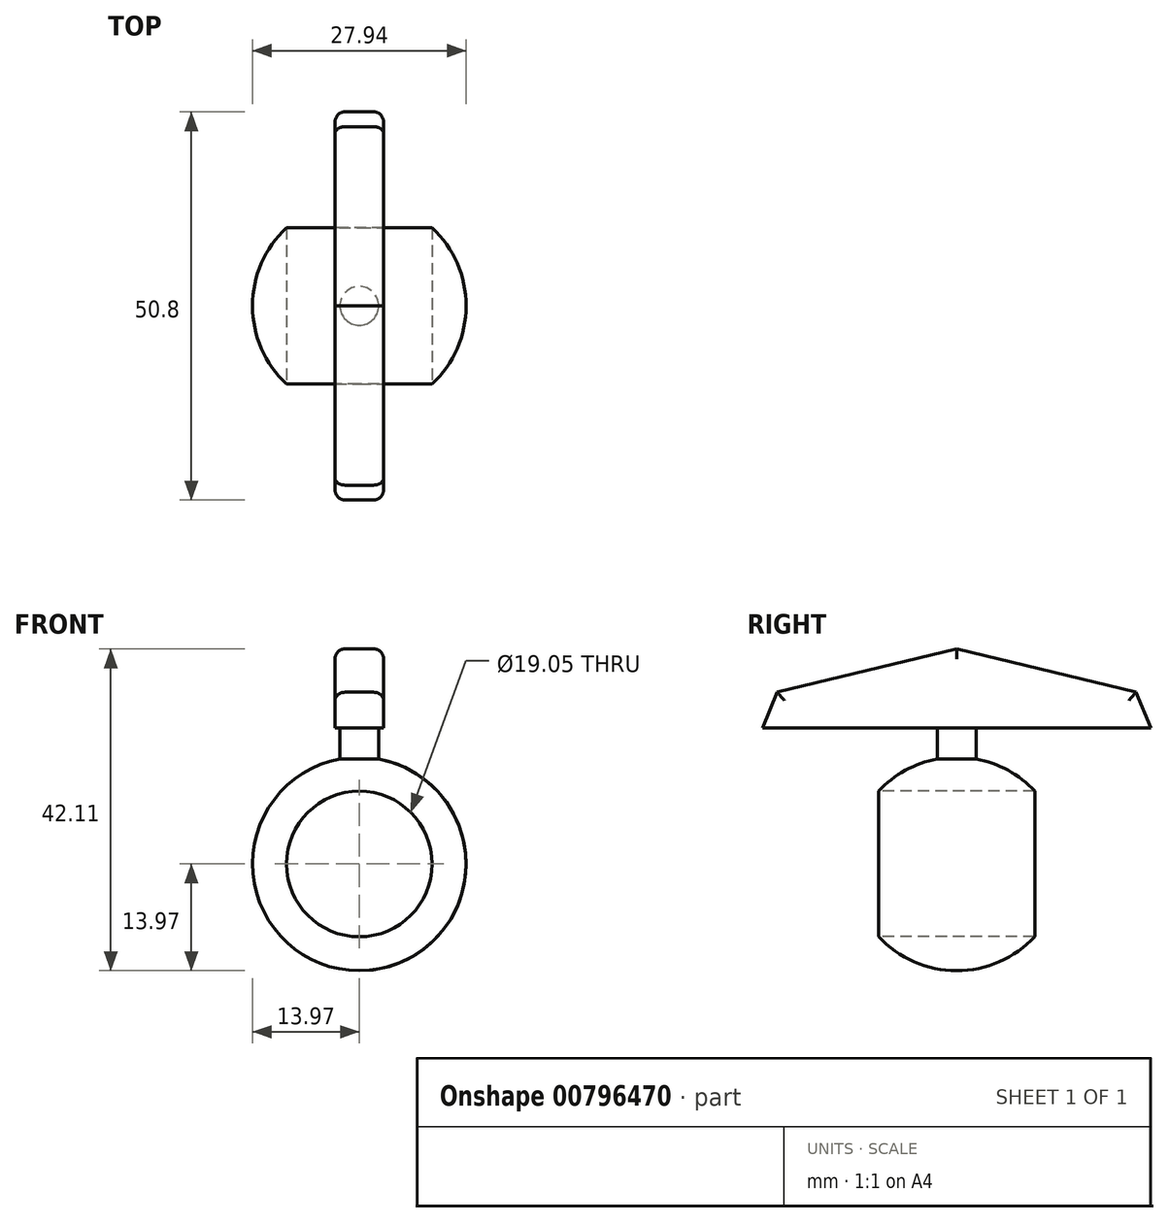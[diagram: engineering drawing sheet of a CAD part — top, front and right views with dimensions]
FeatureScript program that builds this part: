
annotation { "Feature Type Name" : "Feature", "Feature Type Description" : "" }
export const myFeature = defineFeature(function(context is Context, id is Id, definition is map)
    precondition{}
    {
        {
            var Q0;
            Q0=qCreatedBy(makeId("Front.planeOp"),FACE);
            var sketch = newSketch(context, id + "F0", { "sketchPlane" : qUnion([Q0])});
            skLineSegment(sketch, "E0", {"start": v(0, 13.97) * mm, "end": v(0, -13.97) * mm});
            skArc(sketch, "E1", {"start": v(0, -13.97) * mm, "mid": v(13.97, 0) * mm, "end": v(0, 13.97) * mm});
            skLineSegment(sketch, "E2", {"start": v(0, 13.97) * mm, "end": v(0, 17.78) * mm});
            skLineSegment(sketch, "E3", {"start": v(0, 17.78) * mm, "end": v(2.54, 17.78) * mm});
            skLineSegment(sketch, "E4", {"start": v(2.54, 17.78) * mm, "end": v(2.54, 13.74) * mm});
            skSolve(sketch);
        }
        {
            var Q0;
            Q0=qCreatedBy(makeId("Front.planeOp"),FACE);
            var sketch = newSketch(context, id + "F1", { "sketchPlane" : qUnion([Q0])});
            skLineSegment(sketch, "E5", {"start": v(0, 0) * mm, "end": v(0, 12.7) * mm});
            skSolve(sketch);
        }
        {
            var Q0;
            Q0=makeQuery(id+"F0.imprint","IMPRINT",FACE,{"disambiguationData":[TD([[makeQuery(id+"F0.imprint","IMPRINT",EDGE,{"derivedFrom":sQuery(id+"F0.wireOp",EDGE,"E0")}),1.0]])]});
            var Q1;
            {var subQ0=sQuery(id+"F0.wireOp",EDGE,"E2");Q1=makeQuery(id+"F0.imprint","IMPRINT",FACE,{"disambiguationData":[TD([[makeQuery(id+"F0.imprint","IMPRINT",EDGE,{"derivedFrom":subQ0}),-1.0]])]});}
            var Q2;
            Q2=sQuery(id+"F1.wireOp",EDGE,"E5");
            revolve(context, id + "F2", {"surfaceOperationType" : NewSurfaceOperationType.NEW, "entities" : qUnion([Q0, Q1]), "axis" : qUnion([Q2]), "revolveType" : RevolveType.FULL});
        }
        {
            var Q0;
            Q0=sQuery(id+"F1.wireOp",VERTEX,"E5.start");
            var Q1;
            Q1=makeQuery(id+"F2.opRevolve","SWEPT_BODY",BODY,{"disambiguationData":[OSD([sQuery(id+"F0.wireOp",EDGE,"E0"),sQuery(id+"F0.wireOp",EDGE,"E1")])]});
            hole(context, id + "F3", {"style" : HoleStyle.SIMPLE, "endStyle" : HoleEndStyle.BLIND, "holeDiameter" : 19.05 * mm, "majorDiameter" : 6.35 * mm, "holeDepth" : 25.4 * mm, "isTappedThrough" : true, "tappedDepth" : 12.7 * mm, "tapClearance" : 3, "locations" : qUnion([Q0]), "scope" : qUnion([Q1])});
        }
        {
            var Q0;
            Q0=sQuery(id+"F1.wireOp",VERTEX,"E5.start");
            var Q1;
            Q1=makeQuery(id+"F2.opRevolve","SWEPT_BODY",BODY,{"disambiguationData":[OSD([sQuery(id+"F0.wireOp",EDGE,"E0"),sQuery(id+"F0.wireOp",EDGE,"E1")])]});
            hole(context, id + "F4", {"style" : HoleStyle.SIMPLE, "endStyle" : HoleEndStyle.BLIND, "oppositeDirection" : true, "holeDiameter" : 19.05 * mm, "majorDiameter" : 6.35 * mm, "holeDepth" : 25.4 * mm, "isTappedThrough" : true, "tappedDepth" : 12.7 * mm, "tapClearance" : 3, "locations" : qUnion([Q0]), "scope" : qUnion([Q1])});
        }
        {
            var Q0;
            Q0=qCreatedBy(makeId("Right.planeOp"),FACE);
            var sketch = newSketch(context, id + "F5", { "sketchPlane" : qUnion([Q0])});
            skLineSegment(sketch, "E6", {"start": v(0, 17.78) * mm, "end": v(25.4, 17.78) * mm});
            skLineSegment(sketch, "E7", {"start": v(25.4, 17.78) * mm, "end": v(23.45, 22.47) * mm});
            skLineSegment(sketch, "E8", {"start": v(23.45, 22.47) * mm, "end": v(0, 28.14) * mm});
            skLineSegment(sketch, "E9", {"start": v(0, 28.14) * mm, "end": v(0, 17.78) * mm});
            skLineSegment(sketch, "E10.MirrorCS", {"start": v(-23.45, 22.47) * mm, "end": v(0, 28.14) * mm});
            skLineSegment(sketch, "E11.MirrorCS", {"start": v(-25.4, 17.78) * mm, "end": v(-23.45, 22.47) * mm});
            skLineSegment(sketch, "E12.MirrorCS", {"start": v(0, 17.78) * mm, "end": v(-25.4, 17.78) * mm});
            skSolve(sketch);
        }
        {
            var Q0;
            Q0 = qSketchRegion(id + "F5", true);
            extrude(context, id + "F6", {"entities" : qUnion([Q0]), "operationType" : NewBodyOperationType.ADD, "endBound" : BoundingType.SYMMETRIC, "depth" : 6.35 * mm, "offsetDistance" : 25.4 * mm});
        }
        {
            var Q0;
            Q0=makeQuery(id+"F6.opExtrude","CAP_EDGE",EDGE,{"disambiguationData":[OSD([sQuery(id+"F5.wireOp",EDGE,"E10.MirrorCS")])],"isStart":false});
            var Q1;
            Q1=makeQuery(id+"F6.opExtrude","CAP_EDGE",EDGE,{"disambiguationData":[OSD([sQuery(id+"F5.wireOp",EDGE,"E10.MirrorCS")])],"isStart":true});
            var Q2;
            Q2=makeQuery(id+"F6.opExtrude","CAP_EDGE",EDGE,{"disambiguationData":[OSD([sQuery(id+"F5.wireOp",EDGE,"E8")])],"isStart":false});
            var Q3;
            Q3=makeQuery(id+"F6.opExtrude","CAP_EDGE",EDGE,{"disambiguationData":[OSD([sQuery(id+"F5.wireOp",EDGE,"E8")])],"isStart":true});
            var Q4;
            Q4=makeQuery(id+"F6.opExtrude","CAP_EDGE",EDGE,{"disambiguationData":[OSD([sQuery(id+"F5.wireOp",EDGE,"E7")])],"isStart":false});
            var Q5;
            Q5=makeQuery(id+"F6.opExtrude","CAP_EDGE",EDGE,{"disambiguationData":[OSD([sQuery(id+"F5.wireOp",EDGE,"E11.MirrorCS")])],"isStart":false});
            var Q6;
            Q6=makeQuery(id+"F6.opExtrude","CAP_EDGE",EDGE,{"disambiguationData":[OSD([sQuery(id+"F5.wireOp",EDGE,"E11.MirrorCS")])],"isStart":true});
            var Q7;
            Q7=makeQuery(id+"F6.opExtrude","CAP_EDGE",EDGE,{"disambiguationData":[OSD([sQuery(id+"F5.wireOp",EDGE,"E7")])],"isStart":true});
            fillet(context, id + "F7", {"entities" : qUnion([Q0, Q1, Q2, Q3, Q4, Q5, Q6, Q7]), "radius" : 1.27 * mm, "tangentPropagation" : true, "allowEdgeOverflow" : false});
        }
    });
